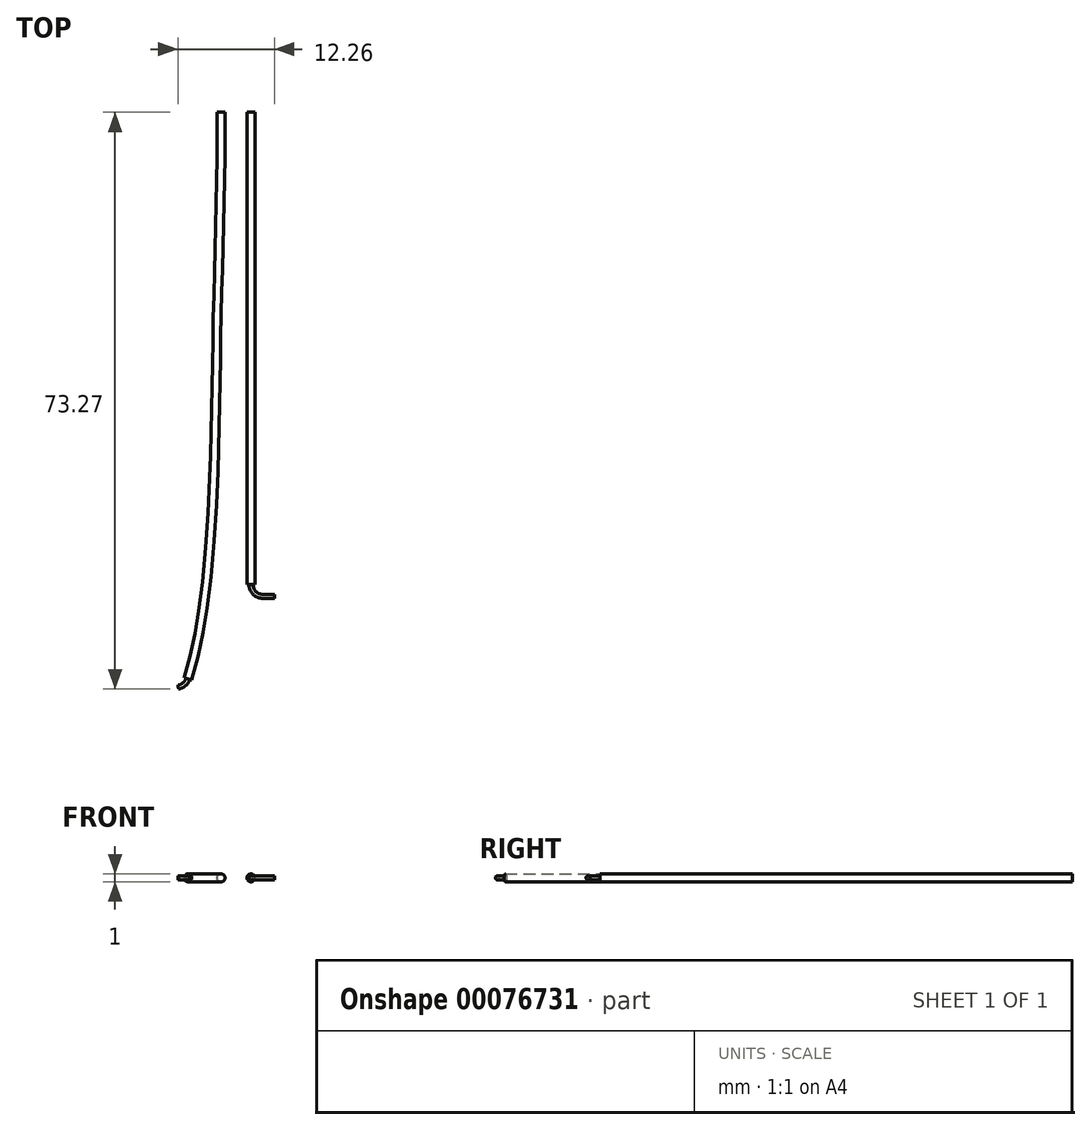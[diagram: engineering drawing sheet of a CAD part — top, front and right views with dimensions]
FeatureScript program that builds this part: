
annotation { "Feature Type Name" : "Feature", "Feature Type Description" : "" }
export const myFeature = defineFeature(function(context is Context, id is Id, definition is map)
    precondition{}
    {
        {
            var Q0;
            Q0=qCreatedBy(makeId("Top.planeOp"),FACE);
            var sketch = newSketch(context, id + "F0", { "sketchPlane" : qUnion([Q0])});
            skLineSegment(sketch, "E0", {"start": v(0, 0) * mm, "end": v(0, 60) * mm});
            skFitSpline(sketch, "E1", {"points": [v(-8, -12) * mm, v(-4.32, 31.63) * mm, v(-3.81, 60) * mm], "startDerivative": vector(18.87, 58.22) * mm, "endDerivative": vector(-0.55, 75.04) * mm});
            skLineSegment(sketch, "E2", {"start": v(1.5, -1.5) * mm, "end": v(3, -1.5) * mm});
            skArc(sketch, "E3", {"start": v(0, 0) * mm, "mid": v(0.44, -1.06) * mm, "end": v(1.5, -1.5) * mm});
            skArc(sketch, "E4", {"start": v(-8, -12) * mm, "mid": v(-8.47, -12.69) * mm, "end": v(-9.23, -13.02) * mm});
            skLineSegment(sketch, "E5", {"start": v(-9.23, -13.02) * mm, "end": v(-6.85, -12.7) * mm, "construction": true});
            skLineSegment(sketch, "E6", {"start": v(-9.23, -13.02) * mm, "end": v(-9.23, -10.46) * mm, "construction": true});
            skSolve(sketch);
        }
        {
            var Q0;
            Q0=qCreatedBy(makeId("Front.planeOp"),FACE);
            var Q1;
            Q1=sQuery(id+"F0.wireOp",VERTEX,"E0.end");
            cPlane(context, id + "F1", {"entities" : qUnion([Q0, Q1]), "cplaneType" : CPlaneType.PLANE_POINT, "offset" : 60 * mm, "oppositeDirection" : true, "width" : 150 * mm, "height" : 150 * mm});
        }
        {
            var Q0;
            Q0=qCreatedBy(id+"F1.planeOp",FACE);
            var sketch = newSketch(context, id + "F2", { "sketchPlane" : qUnion([Q0])});
            skCircle(sketch, "E7", {"center": v(0, 0) * mm, "radius": 0.5 * mm});
            skCircle(sketch, "E8", {"center": v(-3.81, 0) * mm, "radius": 0.5 * mm});
            skSolve(sketch);
        }
        {
            var Q0;
            Q0=makeQuery(id+"F2.imprint","IMPRINT",FACE,{"disambiguationData":[TD([[makeQuery(id+"F2.imprint","IMPRINT",EDGE,{"derivedFrom":sQuery(id+"F2.wireOp",EDGE,"E7")}),1.0]])]});
            var Q1;
            Q1=sQuery(id+"F0.wireOp",EDGE,"E0");
            sweep(context, id + "F3", {"profiles" : qUnion([Q0]), "path" : qUnion([Q1])});
        }
        {
            var Q0;
            Q0=makeQuery(id+"F2.imprint","IMPRINT",FACE,{"disambiguationData":[TD([[makeQuery(id+"F2.imprint","IMPRINT",EDGE,{"derivedFrom":sQuery(id+"F2.wireOp",EDGE,"E8")}),1.0]])]});
            var Q1;
            Q1=sQuery(id+"F0.wireOp",EDGE,"E1");
            sweep(context, id + "F4", {"profiles" : qUnion([Q0]), "path" : qUnion([Q1])});
        }
        {
            var Q0;
            Q0=makeQuery(id+"F3.opSweep","CAP_FACE",FACE,{"disambiguationData":[OSD([sQuery(id+"F0.wireOp",VERTEX,"E0.start"),sQuery(id+"F2.wireOp",EDGE,"E7")])],"isStart":false});
            var sketch = newSketch(context, id + "F5", { "sketchPlane" : qUnion([Q0])});
            skCircle(sketch, "E9", {"center": v(0, 0) * mm, "radius": 0.25 * mm});
            skSolve(sketch);
        }
        {
            var Q0;
            Q0=makeQuery(id+"F5.imprint","IMPRINT",FACE,{"disambiguationData":[TD([[makeQuery(id+"F5.imprint","IMPRINT",EDGE,{"derivedFrom":sQuery(id+"F5.wireOp",EDGE,"E9")}),1.0]])]});
            var Q1;
            Q1=sQuery(id+"F0.wireOp",EDGE,"E3");
            var Q2;
            Q2=sQuery(id+"F0.wireOp",EDGE,"E2");
            sweep(context, id + "F6", {"profiles" : qUnion([Q0]), "path" : qUnion([Q1, Q2])});
        }
        {
            var Q0;
            Q0=makeQuery(id+"F4.opSweep","CAP_FACE",FACE,{"disambiguationData":[OSD([sQuery(id+"F0.wireOp",VERTEX,"E1.start"),sQuery(id+"F2.wireOp",EDGE,"E8")])],"isStart":false});
            var sketch = newSketch(context, id + "F7", { "sketchPlane" : qUnion([Q0])});
            skCircle(sketch, "E10", {"center": v(-3.81, 0) * mm, "radius": 0.25 * mm});
            skSolve(sketch);
        }
        {
            var Q0;
            Q0=makeQuery(id+"F7.imprint","IMPRINT",FACE,{"disambiguationData":[TD([[makeQuery(id+"F7.imprint","IMPRINT",EDGE,{"derivedFrom":sQuery(id+"F7.wireOp",EDGE,"E10")}),1.0]])]});
            var Q1;
            Q1=sQuery(id+"F0.wireOp",EDGE,"E4");
            sweep(context, id + "F8", {"profiles" : qUnion([Q0]), "path" : qUnion([Q1])});
        }
    });
